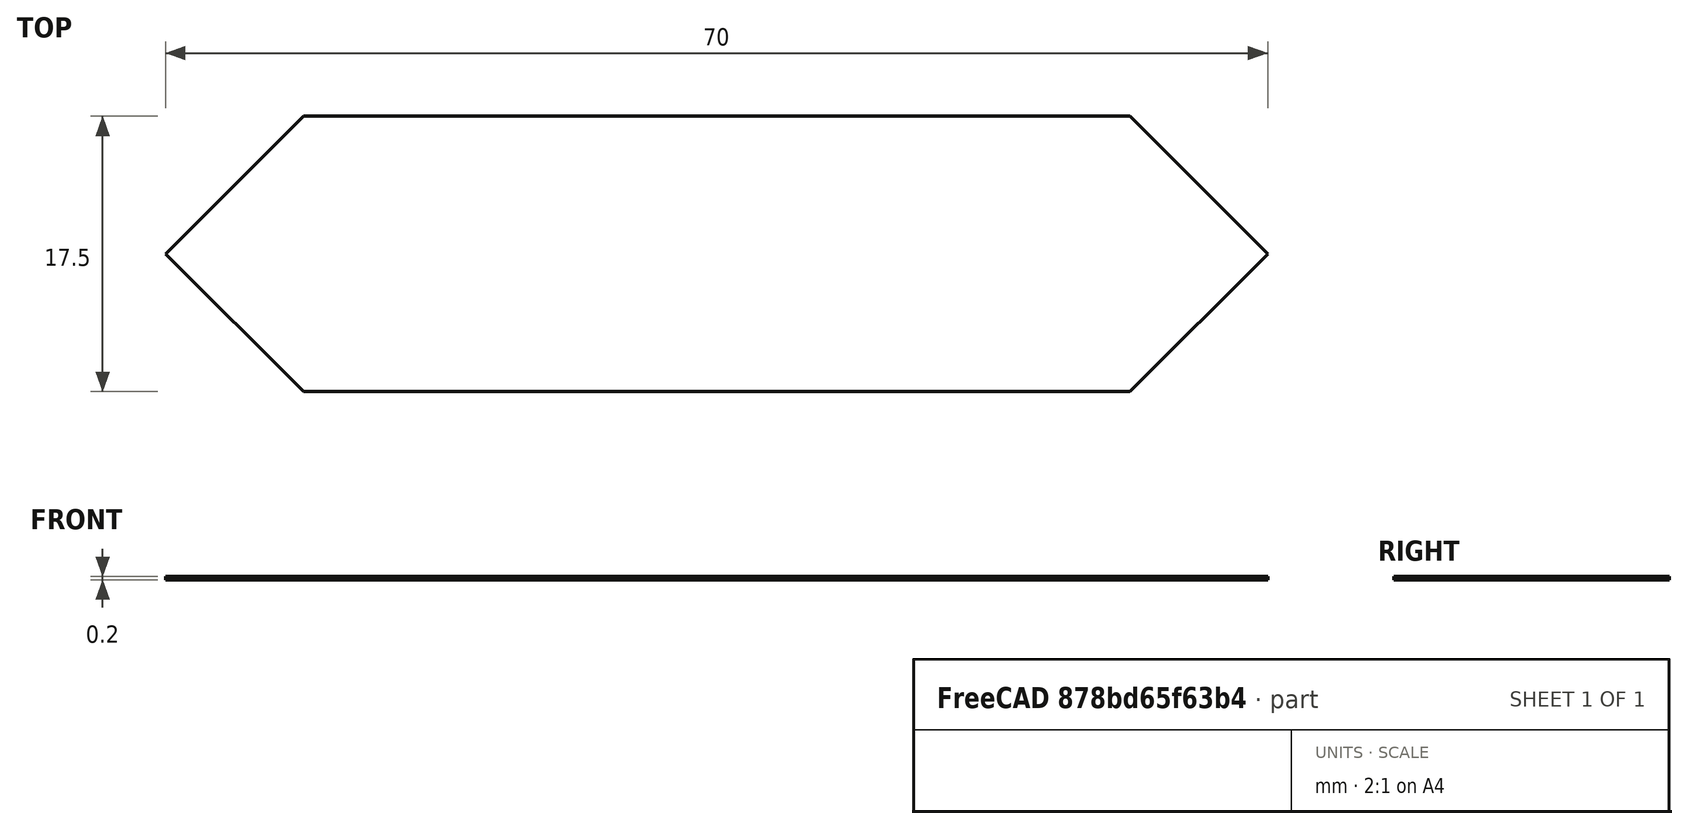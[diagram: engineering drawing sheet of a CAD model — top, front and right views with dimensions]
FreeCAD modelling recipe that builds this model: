
FCSTD DOCUMENT  (FreeCAD 0.20R29603 (Git))
Label: FacePlate_80x20
License: All rights reserved
LicenseURL: http://en.wikipedia.org/wiki/All_rights_reserved
objects: Sketcher::SketchObject×1, PartDesign::Pad×1, PartDesign::Body×1
note: 4 computed .brp shape members not serialized (recipe doc carries the construction recipe); baked Part::Feature solids carry a one-line shape summary decoded from their .brp

FEATURE [Sketcher::SketchObject] Sketch
  FullyConstrained = true
  MapMode = 5
  Support = -> [XY_Plane]
  sketch-geometry (6):
    g0: LineSegment StartX=-26.25 StartY=8.75 StartZ=0 EndX=26.25 EndY=8.75 EndZ=0
    g1: LineSegment StartX=-26.25 StartY=-8.75 StartZ=0 EndX=26.25 EndY=-8.75 EndZ=0
    g2: LineSegment StartX=26.25 StartY=8.75 StartZ=0 EndX=35 EndY=0 EndZ=0
    g3: LineSegment StartX=26.25 StartY=-8.75 StartZ=0 EndX=35 EndY=0 EndZ=0
    g4: LineSegment StartX=-26.25 StartY=-8.75 StartZ=0 EndX=-35 EndY=0 EndZ=0
    g5: LineSegment StartX=-26.25 StartY=8.75 StartZ=0 EndX=-35 EndY=0 EndZ=0
  constraints (16):
    c: Horizontal(g0)
    c: Horizontal(g1)
    c: Coincident(g2,g0)
    c: PointOnObject(g2,g-1)
    c: Coincident(g3,g1)
    c: Coincident(g3,g2)
    c: Coincident(g4,g1)
    c: Coincident(g5,g0)
    c: Coincident(g5,g4)
    c: Angle(g4,g5) = 1.5708
    c: DistanceY(g1,g0) = 17.5
    c: Angle(g2,g3) = 1.5708
    c: Symmetric(g0,g1,g-1)
    c: Equal(g0,g1)
    c: Symmetric(g4,g2,g-2)
    c: DistanceX(g4,g2) = 70
FEATURE [PartDesign::Pad] Pad  label="Face"
  Direction = (0,0,1)
  Length = 0.2
  Length2 = 100
  Profile = -> Sketch
  Type = 0
FEATURE [PartDesign::Body] Body
  Group = -> [Sketch,Pad]
  Origin = -> Origin
  Tip = -> Pad
